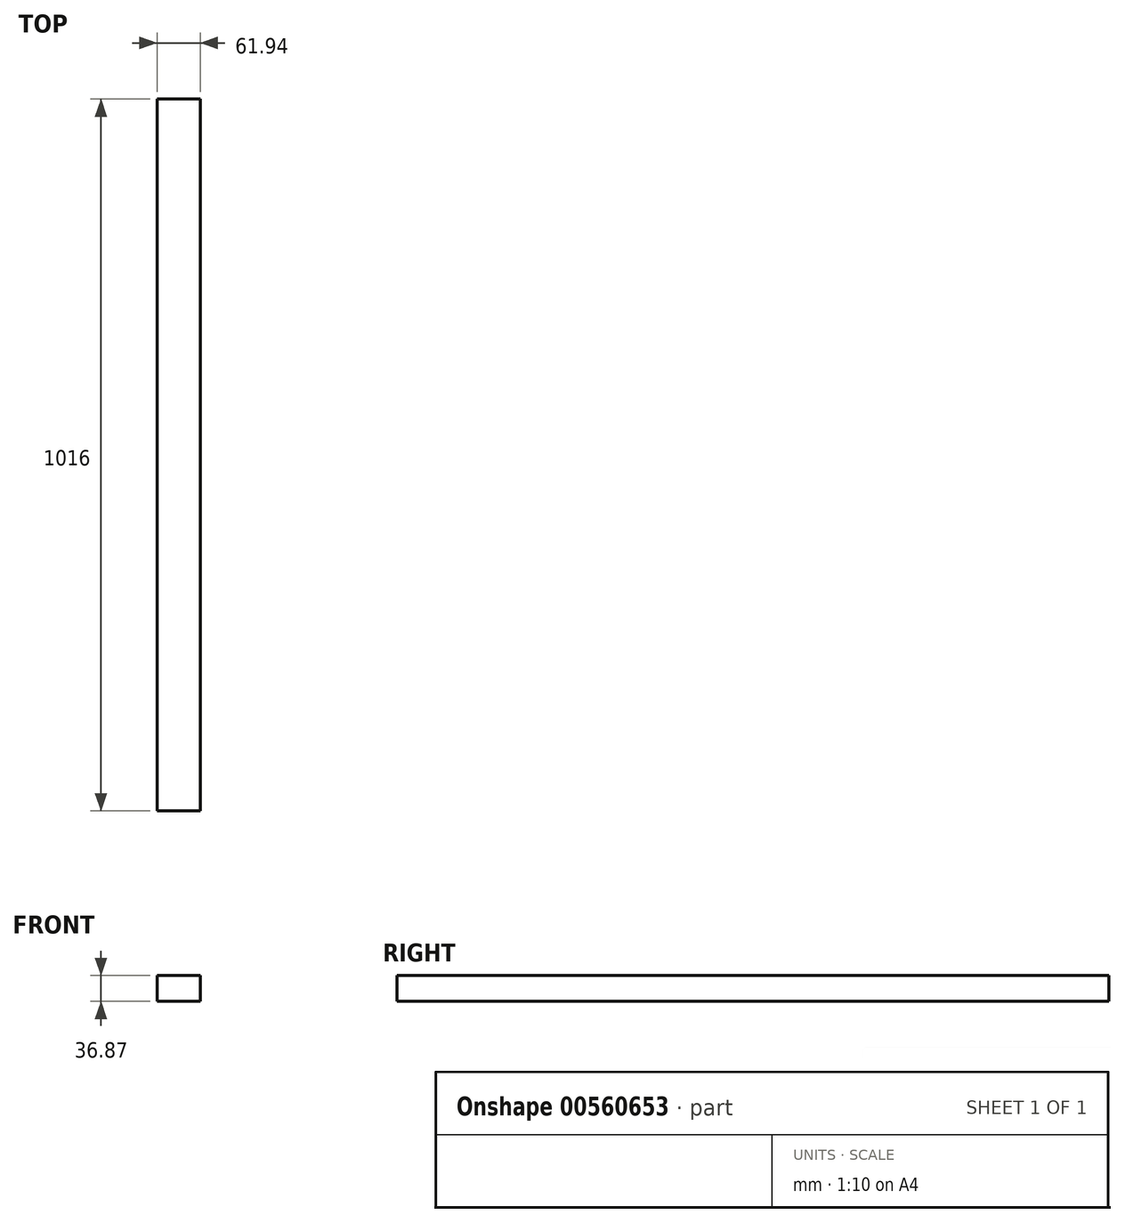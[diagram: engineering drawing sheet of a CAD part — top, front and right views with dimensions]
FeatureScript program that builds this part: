
annotation { "Feature Type Name" : "Feature", "Feature Type Description" : "" }
export const myFeature = defineFeature(function(context is Context, id is Id, definition is map)
    precondition{}
    {
        {
            var Q0;
            Q0=qCreatedBy(makeId("Front.planeOp"),FACE);
            var sketch = newSketch(context, id + "F0", { "sketchPlane" : qUnion([Q0])});
            skLineSegment(sketch, "E0.bottom", {"start": v(0, 0) * mm, "end": v(-61.94, 0) * mm});
            skLineSegment(sketch, "E0.top", {"start": v(0, -36.87) * mm, "end": v(-61.94, -36.87) * mm});
            skLineSegment(sketch, "E0.left", {"start": v(0, 0) * mm, "end": v(0, -36.87) * mm});
            skLineSegment(sketch, "E0.right", {"start": v(-61.94, 0) * mm, "end": v(-61.94, -36.87) * mm});
            skSolve(sketch);
        }
        {
            var Q0;
            Q0=makeQuery(id+"F0.imprint","IMPRINT",FACE,{"disambiguationData":[TD([[makeQuery(id+"F0.imprint","IMPRINT",EDGE,{"derivedFrom":sQuery(id+"F0.wireOp",EDGE,"E0.bottom")}),1.0]])]});
            extrude(context, id + "F1", {"entities" : qUnion([Q0]), "depth" : 1016 * mm, "offsetDistance" : 25.4 * mm});
        }
    });
